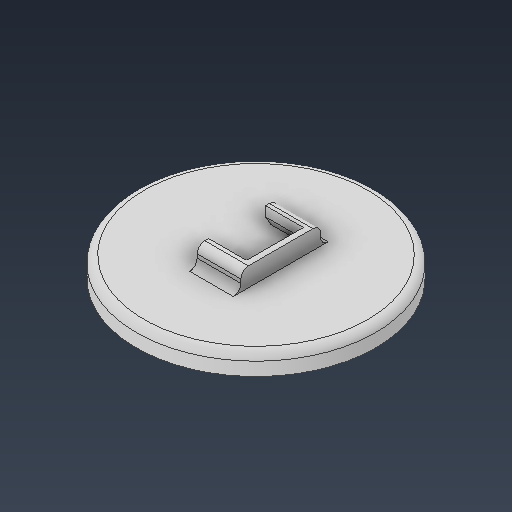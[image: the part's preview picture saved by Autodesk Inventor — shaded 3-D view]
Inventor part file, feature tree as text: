
AUTODESK INVENTOR PART (.ipt)
format: ipt  version: 2025.3 (Build 293356000, 356)  size: 272,384 bytes
history: native  units: mm
features: sketch x6, extrude x6, fillet x2, projected_geometry x2, other x1
ambient origin geometry x8: Origin, YZ Plane, XZ Plane, XY Plane, X Axis, Y Axis, Z Axis, Center Point
bodies: Body1 (feature_tree)
feature tree (17):
  other  "實體1"
  sketch  "草圖1"
  extrude  "支撐處(低一點)"  Depth=58.0mm
  extrude  "框架"  Depth=43.0mm
  extrude  "底盤"  Depth=44.0mm
  extrude  "填中空"  Depth=56.0mm
  fillet  "圓角2"  Radius=27.0mm
  extrude  "擠出4"  Depth=22.8mm
  fillet  "圓角3"  Radius=6.806784mm
  extrude  "擠出5"  Depth=1.3mm
  sketch  "草圖2"
  sketch  "草圖3"
  sketch  "草圖4"
  sketch  "草圖5"
  projected_geometry  "投影迴路1"
  projected_geometry  "投影迴路2"
  sketch  "草圖6"
